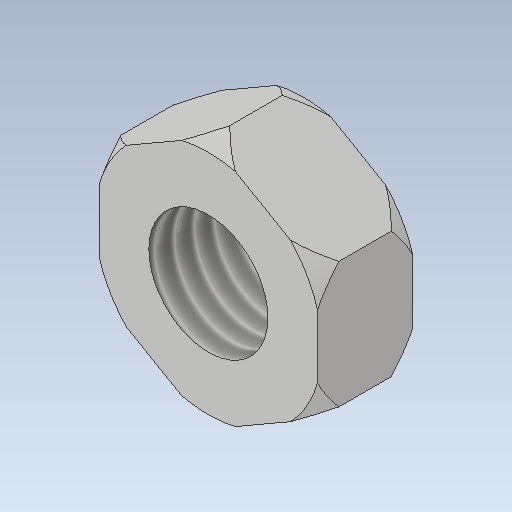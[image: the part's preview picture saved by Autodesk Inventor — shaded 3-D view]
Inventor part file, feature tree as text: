
AUTODESK INVENTOR PART (.ipt)
format: ipt  version: 2020 (Build 240168000, 168)  size: 141,312 bytes
history: native  units: mm
features: sketch x2, other x1, revolve x1, extrude x1, thread x1
ambient origin geometry x8: Origin, YZ Plane, XZ Plane, XY Plane, X Axis, Y Axis, Z Axis, Center Point
bodies: Body1 (feature_tree)
feature tree (6):
  other  "Твердое тело1"
  revolve  "Вращение1"
  extrude  "Выдавливание1"  TaperAngle=90.0deg  [1 undecoded]
  thread  "Резьба1"
  sketch  "Эскиз1"
  sketch  "Эскиз2"
note: 1 required parameter value undecoded (feature->parameter linkage not recoverable at this tier; creation-order binding heuristic only, values carry confidence <= 0.55)
